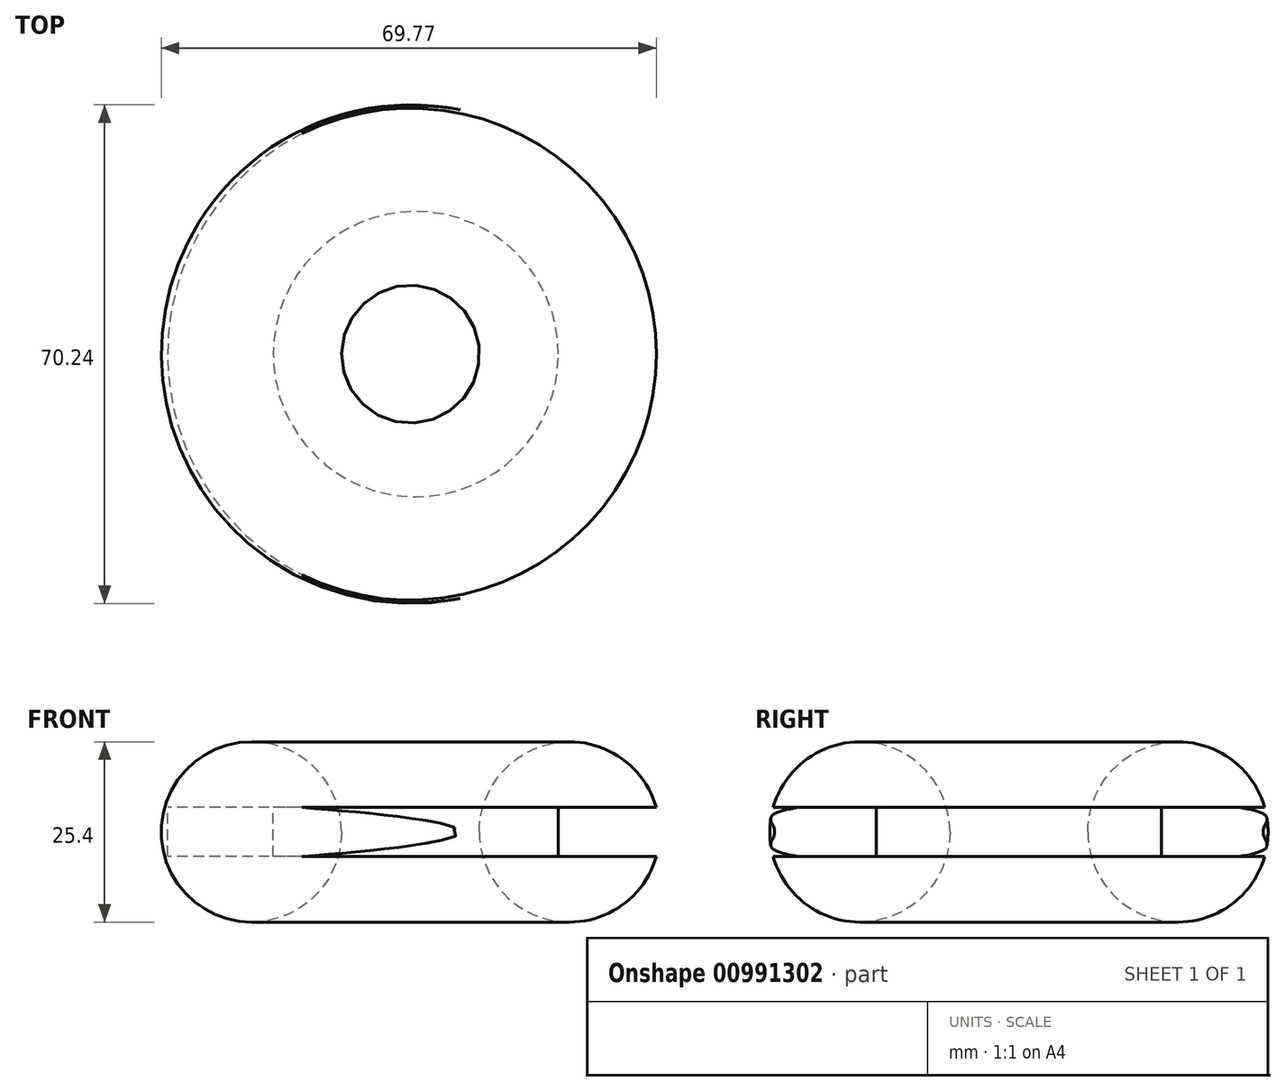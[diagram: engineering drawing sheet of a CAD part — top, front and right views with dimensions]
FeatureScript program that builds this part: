
annotation { "Feature Type Name" : "Feature", "Feature Type Description" : "" }
export const myFeature = defineFeature(function(context is Context, id is Id, definition is map)
    precondition{}
    {
        {
            var Q0;
            Q0=qCreatedBy(makeId("Front.planeOp"),FACE);
            var sketch = newSketch(context, id + "F0", { "sketchPlane" : qUnion([Q0])});
            skCircle(sketch, "E0", {"center": v(0, 0) * mm, "radius": 12.7 * mm});
            skLineSegment(sketch, "E1", {"start": v(22.42, -10.7) * mm, "end": v(22.42, 34.7) * mm, "construction": true});
            skSolve(sketch);
        }
        {
            var Q0;
            Q0 = qSketchRegion(id + "F0", true);
            var Q1;
            Q1=sQuery(id+"F0.wireOp",EDGE,"E1");
            revolve(context, id + "F1", {"surfaceOperationType" : NewSurfaceOperationType.NEW, "entities" : qUnion([Q0]), "axis" : qUnion([Q1]), "revolveType" : RevolveType.FULL});
        }
        {
            var Q0;
            Q0=qCreatedBy(makeId("Front.planeOp"),FACE);
            var sketch = newSketch(context, id + "F2", { "sketchPlane" : qUnion([Q0])});
            skLineSegment(sketch, "E2.bottom", {"start": v(-11.82, 3.44) * mm, "end": v(3.07, 3.44) * mm});
            skLineSegment(sketch, "E2.top", {"start": v(-11.82, -3.44) * mm, "end": v(3.07, -3.44) * mm});
            skLineSegment(sketch, "E2.left", {"start": v(-11.82, 3.44) * mm, "end": v(-11.82, -3.44) * mm});
            skLineSegment(sketch, "E2.right", {"start": v(3.07, 3.44) * mm, "end": v(3.07, -3.44) * mm});
            skPoint(sketch, "E2.middle", {"position": v(-4.37, 0) * mm});
            skLineSegment(sketch, "E3", {"start": v(23.17, 0) * mm, "end": v(23.17, 39.91) * mm});
            skPoint(sketch, "E3.startSnap0", {"position": v(3.07, 0) * mm});
            skSolve(sketch);
        }
        {
            var Q0;
            Q0 = qSketchRegion(id + "F2", true);
            var Q1;
            Q1=sQuery(id+"F2.wireOp",EDGE,"E3");
            revolve(context, id + "F3", {"operationType" : NewBodyOperationType.REMOVE, "surfaceOperationType" : NewSurfaceOperationType.NEW, "entities" : qUnion([Q0]), "axis" : qUnion([Q1]), "revolveType" : RevolveType.FULL, "oppositeDirection" : true});
        }
    });
